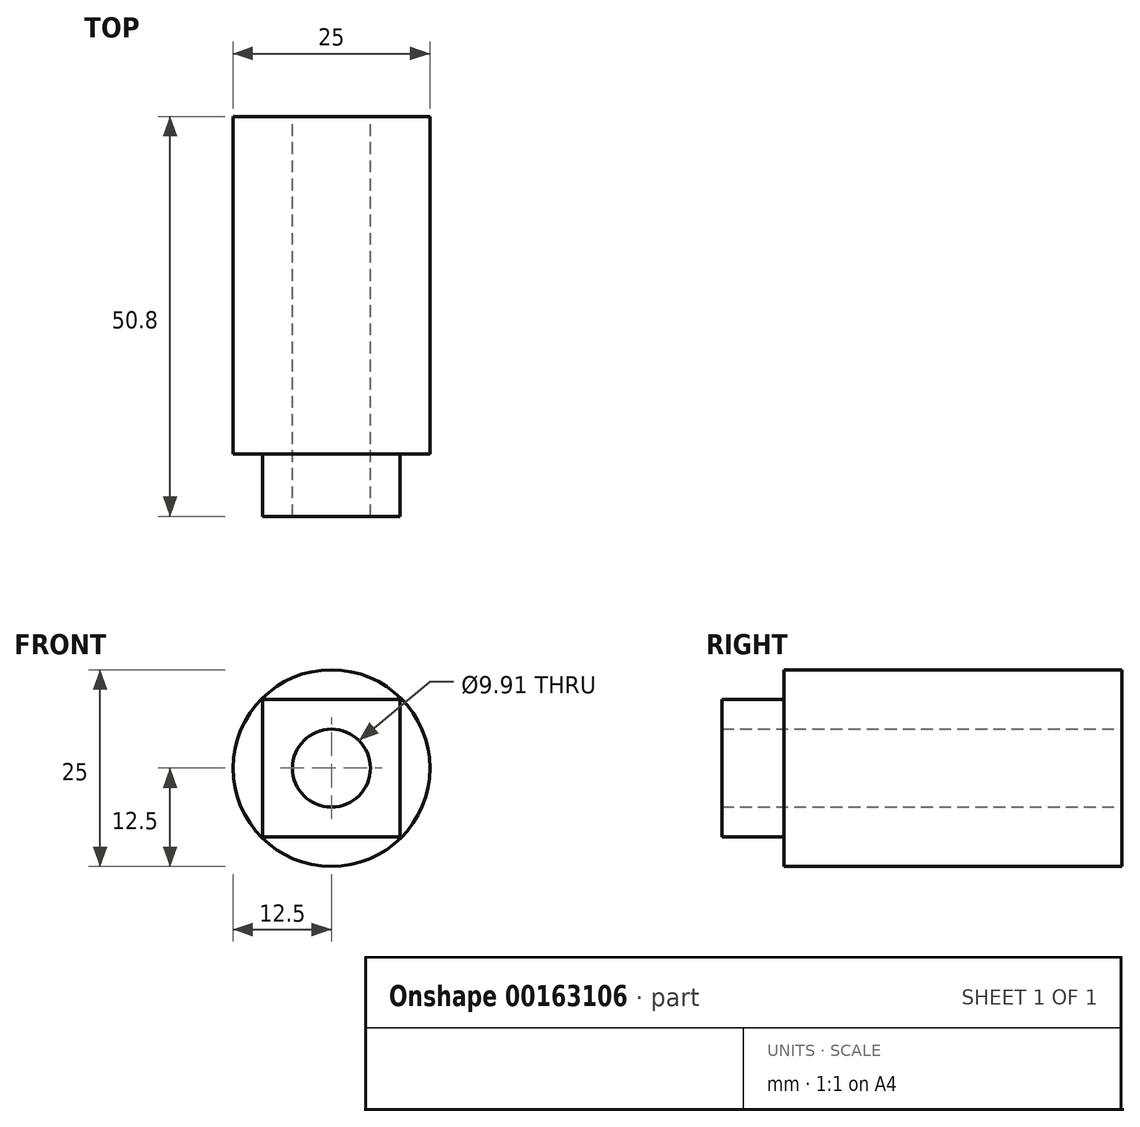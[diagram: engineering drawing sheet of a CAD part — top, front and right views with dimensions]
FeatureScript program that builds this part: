
annotation { "Feature Type Name" : "Feature", "Feature Type Description" : "" }
export const myFeature = defineFeature(function(context is Context, id is Id, definition is map)
    precondition{}
    {
        {
            var Q0;
            Q0=qCreatedBy(makeId("Front.planeOp"),FACE);
            var sketch = newSketch(context, id + "F0", { "sketchPlane" : qUnion([Q0])});
            skCircle(sketch, "E0", {"center": v(0, 0) * mm, "radius": 12.5 * mm});
            skSolve(sketch);
        }
        {
            var Q0;
            Q0=makeQuery(id+"F0.imprint","IMPRINT",FACE,{"disambiguationData":[TD([[makeQuery(id+"F0.imprint","IMPRINT",EDGE,{"derivedFrom":sQuery(id+"F0.wireOp",EDGE,"E0")}),1.0]])]});
            var sketch = newSketch(context, id + "F1", { "sketchPlane" : qUnion([Q0])});
            skLineSegment(sketch, "E1.bottom", {"start": v(8.72, 8.72) * mm, "end": v(-8.72, 8.72) * mm});
            skLineSegment(sketch, "E1.top", {"start": v(8.72, -8.72) * mm, "end": v(-8.72, -8.72) * mm});
            skLineSegment(sketch, "E1.left", {"start": v(8.72, 8.72) * mm, "end": v(8.72, -8.72) * mm});
            skLineSegment(sketch, "E1.right", {"start": v(-8.72, 8.72) * mm, "end": v(-8.72, -8.72) * mm});
            skPoint(sketch, "E1.middle", {"position": v(0, 0) * mm});
            skSolve(sketch);
        }
        {
            var Q0;
            Q0 = qSketchRegion(id + "F0", true);
            extrude(context, id + "F2", {"entities" : qUnion([Q0]), "oppositeDirection" : true, "depth" : 42.9 * mm});
        }
        {
            var Q0;
            Q0 = qSketchRegion(id + "F1", true);
            extrude(context, id + "F3", {"entities" : qUnion([Q0]), "operationType" : NewBodyOperationType.ADD, "depth" : 7.9 * mm});
        }
        {
            var Q0;
            Q0=makeQuery(id+"F2.opExtrude","CAP_FACE",FACE,{"disambiguationData":[OSD([sQuery(id+"F0.wireOp",EDGE,"E0")])],"isStart":false});
            var sketch = newSketch(context, id + "F4", { "sketchPlane" : qUnion([Q0])});
            skCircle(sketch, "E2", {"center": v(0, 0) * mm, "radius": 4.95 * mm});
            skSolve(sketch);
        }
        {
            var Q0;
            Q0 = qSketchRegion(id + "F4", true);
            extrude(context, id + "F5", {"entities" : qUnion([Q0]), "operationType" : NewBodyOperationType.REMOVE, "oppositeDirection" : true, "depth" : 76.2 * mm});
        }
    });
